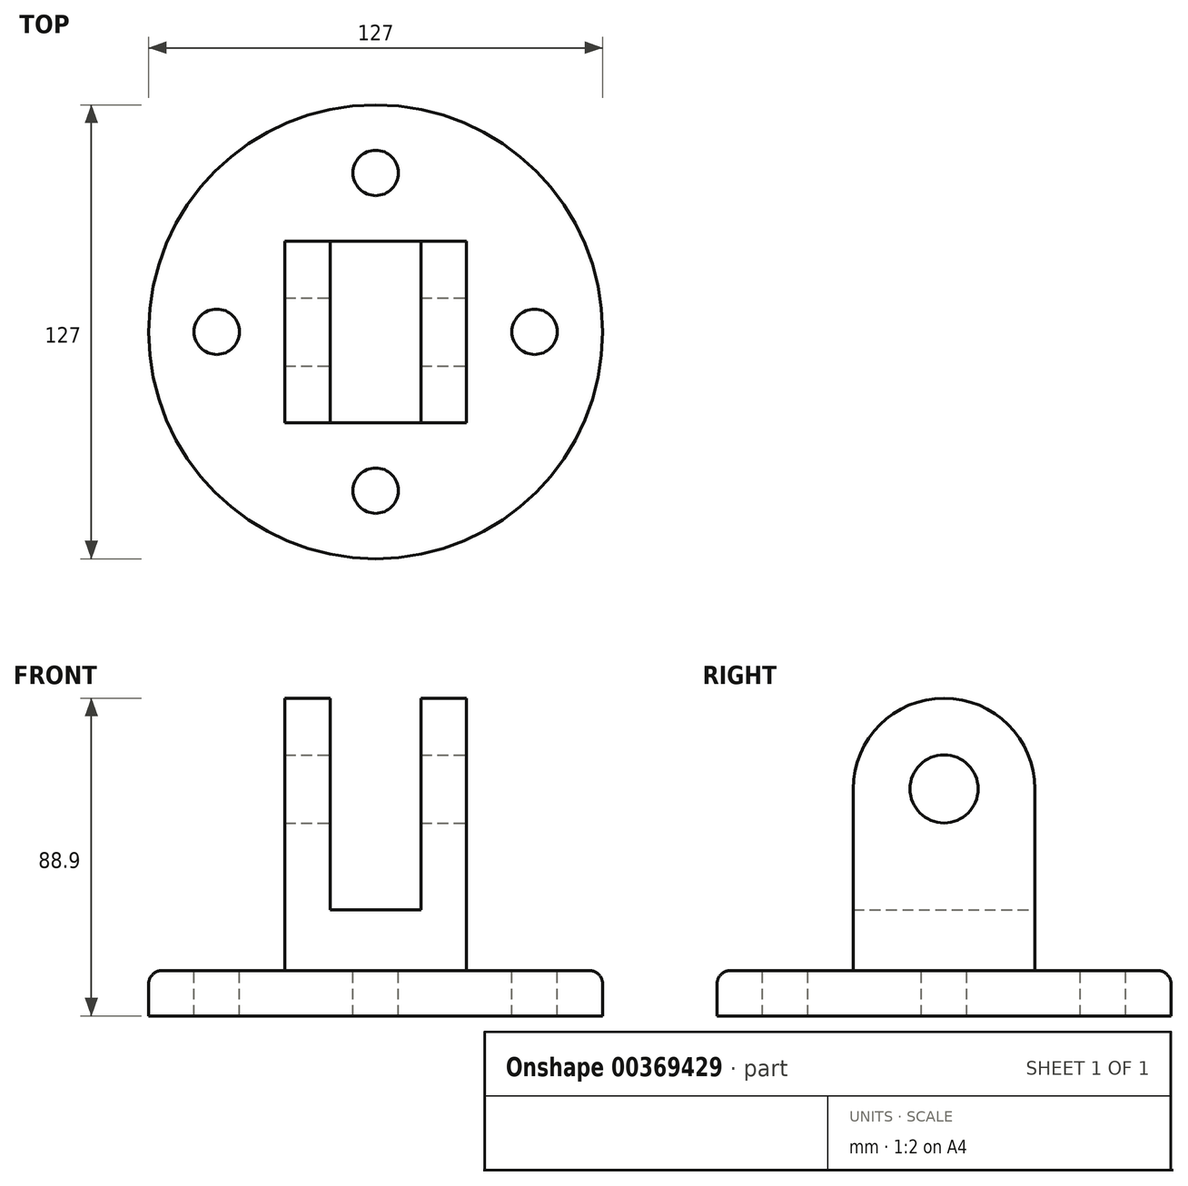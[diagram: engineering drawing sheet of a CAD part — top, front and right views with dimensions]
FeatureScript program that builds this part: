
annotation { "Feature Type Name" : "Feature", "Feature Type Description" : "" }
export const myFeature = defineFeature(function(context is Context, id is Id, definition is map)
    precondition{}
    {
        {
            var Q0;
            Q0=qCreatedBy(makeId("Front.planeOp"),FACE);
            var sketch = newSketch(context, id + "F0", { "sketchPlane" : qUnion([Q0])});
            skLineSegment(sketch, "E0", {"start": v(-38.3, 59.24) * mm, "end": v(-38.3, 0) * mm});
            skLineSegment(sketch, "E1", {"start": v(-38.3, 0) * mm, "end": v(-12.9, 0) * mm});
            skLineSegment(sketch, "E2", {"start": v(-12.9, 0) * mm, "end": v(-12.9, 59.24) * mm});
            skLineSegment(sketch, "E3", {"start": v(-12.9, 59.24) * mm, "end": v(-0.2, 59.24) * mm});
            skLineSegment(sketch, "E4", {"start": v(-0.2, 59.24) * mm, "end": v(-0.2, -16.96) * mm});
            skLineSegment(sketch, "E5", {"start": v(-0.2, -16.96) * mm, "end": v(-51, -16.96) * mm});
            skLineSegment(sketch, "E6", {"start": v(-51, -16.96) * mm, "end": v(-51, 59.24) * mm});
            skLineSegment(sketch, "E7", {"start": v(-51, 59.24) * mm, "end": v(-38.3, 59.24) * mm});
            skSolve(sketch);
        }
        {
            var Q0;
            Q0 = qSketchRegion(id + "F0", true);
            extrude(context, id + "F1", {"entities" : qUnion([Q0]), "depth" : 50.8 * mm});
        }
        {
            var Q0;
            Q0=makeQuery(id+"F1.opExtrude","SWEPT_FACE",FACE,{"disambiguationData":[OSD([sQuery(id+"F0.wireOp",EDGE,"E4")])]});
            var sketch = newSketch(context, id + "F2", { "sketchPlane" : qUnion([Q0])});
            skCircle(sketch, "E8", {"center": v(-25.4, 33.84) * mm, "radius": 25.4 * mm});
            skLineSegment(sketch, "E9", {"start": v(-50.8, 21.14) * mm, "end": v(-50.8, 59.24) * mm});
            skLineSegment(sketch, "E10", {"start": v(-50.8, 59.24) * mm, "end": v(0, 59.24) * mm});
            skLineSegment(sketch, "E11", {"start": v(0, 59.24) * mm, "end": v(0, 21.14) * mm});
            skSolve(sketch);
        }
        {
            var Q0;
            {var subQ0=sQuery(id+"F2.wireOp",EDGE,"E10");var subQ1=sQuery(id+"F2.wireOp",EDGE,"E8");var subQ2=makeQuery(id+"F2.imprint","INTERSECT",VERTEX,{"derivedFrom":[subQ1,subQ0]});Q0=makeQuery(id+"F2.imprint","IMPRINT",FACE,{"disambiguationData":[TD([[makeQuery(id+"F2.imprint","IMPRINT",EDGE,{"disambiguationData":[TD([[subQ2,-1.0]])],"derivedFrom":subQ1}),-1.0]])]});}
            var Q1;
            {var subQ0=sQuery(id+"F2.wireOp",EDGE,"E10");var subQ1=sQuery(id+"F2.wireOp",EDGE,"E8");var subQ2=makeQuery(id+"F2.imprint","INTERSECT",VERTEX,{"derivedFrom":[subQ1,subQ0]});Q1=makeQuery(id+"F2.imprint","IMPRINT",FACE,{"disambiguationData":[TD([[makeQuery(id+"F2.imprint","IMPRINT",EDGE,{"disambiguationData":[TD([[subQ2,1.0]])],"derivedFrom":subQ1}),-1.0]])]});}
            extrude(context, id + "F3", {"entities" : qUnion([Q0, Q1]), "operationType" : NewBodyOperationType.REMOVE, "endBound" : BoundingType.THROUGH_ALL, "oppositeDirection" : true, "depth" : 25.4 * mm});
        }
        {
            var Q0;
            Q0=makeQuery(id+"F1.opExtrude","SWEPT_FACE",FACE,{"disambiguationData":[OSD([sQuery(id+"F0.wireOp",EDGE,"E4")])]});
            var sketch = newSketch(context, id + "F4", { "sketchPlane" : qUnion([Q0])});
            skCircle(sketch, "E12", {"center": v(-25.4, 33.84) * mm, "radius": 9.52 * mm});
            skSolve(sketch);
        }
        {
            var Q0;
            Q0 = qSketchRegion(id + "F4", true);
            extrude(context, id + "F5", {"entities" : qUnion([Q0]), "operationType" : NewBodyOperationType.REMOVE, "endBound" : BoundingType.THROUGH_ALL, "oppositeDirection" : true, "depth" : 25.4 * mm});
        }
        {
            var Q0;
            Q0=makeQuery(id+"F1.opExtrude","SWEPT_FACE",FACE,{"disambiguationData":[OSD([sQuery(id+"F0.wireOp",EDGE,"E5")])]});
            var sketch = newSketch(context, id + "F6", { "sketchPlane" : qUnion([Q0])});
            skCircle(sketch, "E13", {"center": v(-25.6, 25.4) * mm, "radius": 63.5 * mm});
            skPoint(sketch, "E13.centerSnap0", {"position": v(-25.6, 0) * mm});
            skPoint(sketch, "E13.centerSnap1", {"position": v(-0.2, 25.4) * mm});
            skCircle(sketch, "E14", {"center": v(-25.6, 25.4) * mm, "radius": 44.45 * mm});
            skLineSegment(sketch, "E15", {"start": v(62.34, 25.4) * mm, "end": v(-144.1, 25.4) * mm, "construction": true});
            skLineSegment(sketch, "E16", {"start": v(-25.6, 119.05) * mm, "end": v(-25.6, -63.47) * mm, "construction": true});
            skCircle(sketch, "E17", {"center": v(18.84, 25.4) * mm, "radius": 6.35 * mm});
            skCircle(sketch, "E18", {"center": v(-25.6, -19.05) * mm, "radius": 6.35 * mm});
            skCircle(sketch, "E19", {"center": v(-70.06, 25.4) * mm, "radius": 6.35 * mm});
            skCircle(sketch, "E20", {"center": v(-25.6, 69.85) * mm, "radius": 6.35 * mm});
            skSolve(sketch);
        }
        {
            var Q0;
            Q0=makeQuery(id+"F6.imprint","IMPRINT",FACE,{"disambiguationData":[TD([[makeQuery(id+"F6.imprint","IMPRINT",EDGE,{"derivedFrom":sQuery(id+"F6.wireOp",EDGE,"E13")}),1.0]])]});
            var Q1;
            {var subQ0=sQuery(id+"F0.wireOp",EDGE,"E5");Q1=makeQuery(id+"F6.imprint","IMPRINT",FACE,{"disambiguationData":[TD([[makeQuery(id+"F6.imprint","IMPRINT",EDGE,{"derivedFrom":makeQuery(id+"F1.opExtrude","CAP_EDGE",EDGE,{"disambiguationData":[OSD([subQ0])],"isStart":true})}),1.0]])]});}
            var Q2;
            {var subQ0=sQuery(id+"F0.wireOp",EDGE,"E5");Q2=makeQuery(id+"F6.imprint","IMPRINT",FACE,{"disambiguationData":[TD([[makeQuery(id+"F6.imprint","IMPRINT",EDGE,{"derivedFrom":makeQuery(id+"F1.opExtrude","CAP_EDGE",EDGE,{"disambiguationData":[OSD([subQ0])],"isStart":true})}),-1.0]])]});}
            extrude(context, id + "F7", {"entities" : qUnion([Q0, Q1, Q2]), "operationType" : NewBodyOperationType.ADD, "depth" : 12.7 * mm});
        }
        {
            var Q0;
            Q0=makeQuery(id+"F1.opExtrude","SWEPT_EDGE",EDGE,{"disambiguationData":[OSD([sQuery(id+"F0.wireOp",EDGE,"E5"),sQuery(id+"F0.wireOp",EDGE,"E6")])]});
            var Q1;
            Q1=makeQuery(id+"F1.opExtrude","CAP_EDGE",EDGE,{"disambiguationData":[OSD([sQuery(id+"F0.wireOp",EDGE,"E5")])],"isStart":false});
            var Q2;
            Q2=makeQuery(id+"F1.opExtrude","SWEPT_EDGE",EDGE,{"disambiguationData":[OSD([sQuery(id+"F0.wireOp",EDGE,"E4"),sQuery(id+"F0.wireOp",EDGE,"E5")])]});
            var Q3;
            Q3=makeQuery(id+"F1.opExtrude","CAP_EDGE",EDGE,{"disambiguationData":[OSD([sQuery(id+"F0.wireOp",EDGE,"E5")])],"isStart":true});
            var Q4;
            Q4=makeQuery(id+"F7.opExtrude","CAP_EDGE",EDGE,{"disambiguationData":[OSD([sQuery(id+"F6.wireOp",EDGE,"E13")])],"isStart":true});
            fillet(context, id + "F8", {"entities" : qUnion([Q0, Q1, Q2, Q3, Q4]), "radius" : 3.8 * mm, "tangentPropagation" : true, "allowEdgeOverflow" : false});
        }
    });
